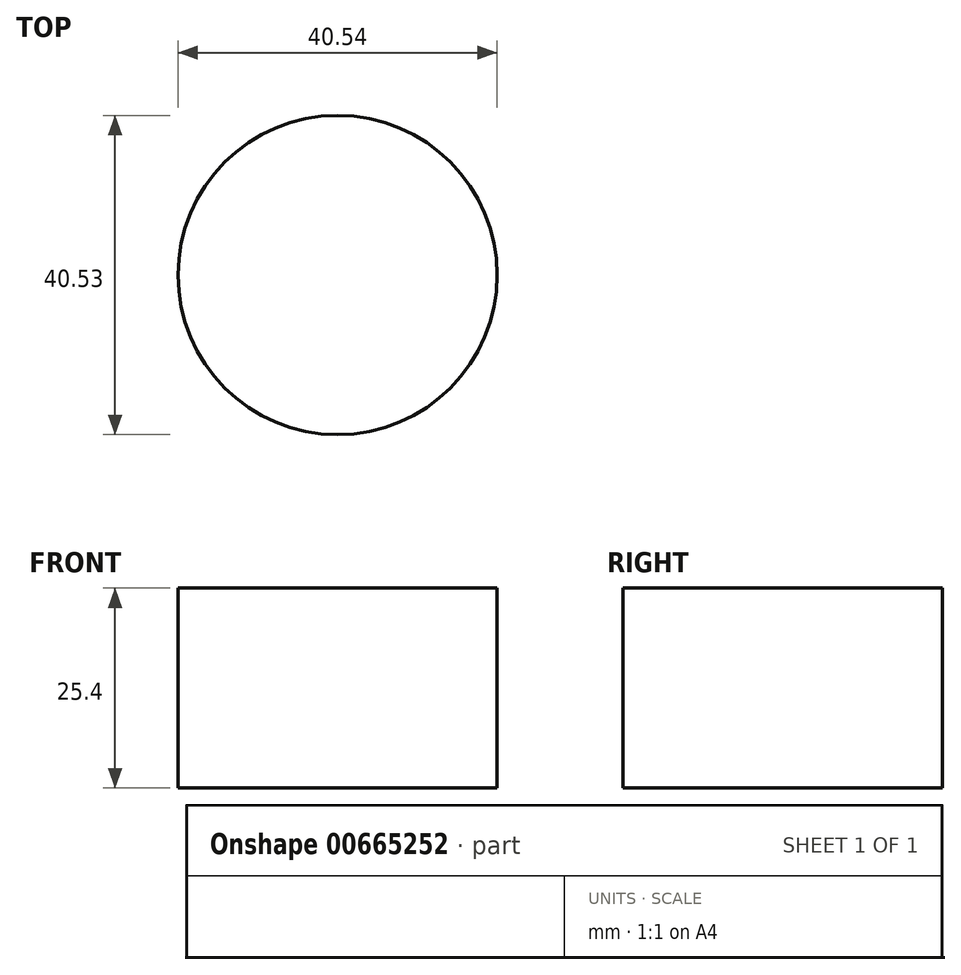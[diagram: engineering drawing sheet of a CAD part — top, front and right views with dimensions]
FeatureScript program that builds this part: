
annotation { "Feature Type Name" : "Feature", "Feature Type Description" : "" }
export const myFeature = defineFeature(function(context is Context, id is Id, definition is map)
    precondition{}
    {
        {
            var Q0;
            Q0=qCreatedBy(makeId("Top.planeOp"),FACE);
            var sketch = newSketch(context, id + "F0", { "sketchPlane" : qUnion([Q0])});
            skCircle(sketch, "E0", {"center": v(-57.37, 57.97) * mm, "radius": 20.27 * mm});
            skSolve(sketch);
        }
        {
            var Q0;
            Q0=sQuery(id+"F0.wireOp",EDGE,"E0");
            extrude(context, id + "F1", {"bodyType" : ToolBodyType.SURFACE, "surfaceEntities" : qUnion([Q0]), "depth" : 25.4 * mm, "offsetDistance" : 25.4 * mm});
        }
    });
